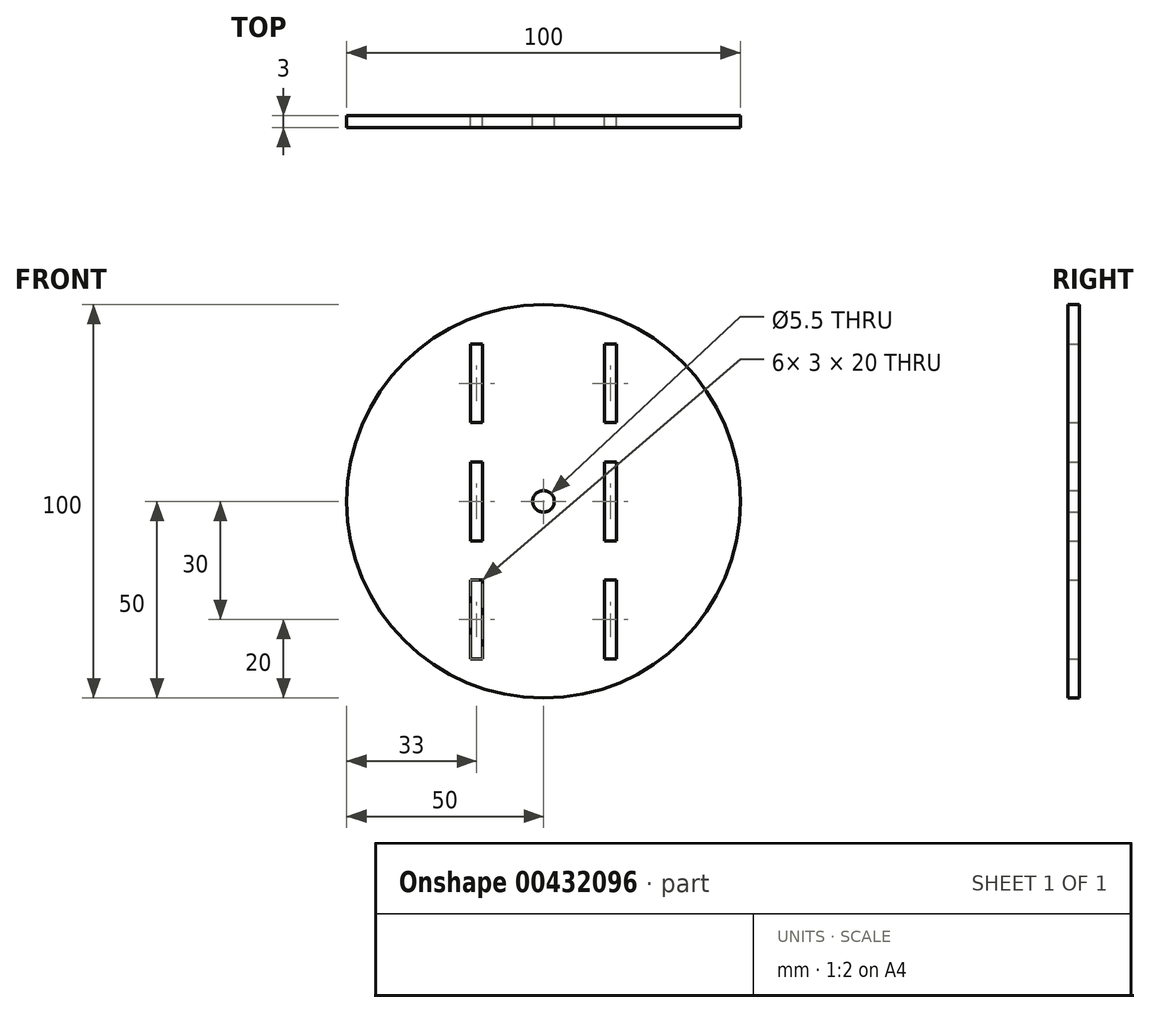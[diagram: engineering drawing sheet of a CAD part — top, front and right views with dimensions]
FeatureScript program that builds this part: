
annotation { "Feature Type Name" : "Feature", "Feature Type Description" : "" }
export const myFeature = defineFeature(function(context is Context, id is Id, definition is map)
    precondition{}
    {
        {
            var Q0;
            Q0=qCreatedBy(makeId("Front.planeOp"),FACE);
            var sketch = newSketch(context, id + "F0", { "sketchPlane" : qUnion([Q0])});
            skCircle(sketch, "E0", {"center": v(0, 0) * mm, "radius": 50 * mm});
            skCircle(sketch, "E1", {"center": v(0, 0) * mm, "radius": 2.75 * mm});
            skLineSegment(sketch, "E2.bottom", {"start": v(-18.5, 10) * mm, "end": v(-15.5, 10) * mm});
            skLineSegment(sketch, "E2.top", {"start": v(-18.5, -10) * mm, "end": v(-15.5, -10) * mm});
            skLineSegment(sketch, "E2.left", {"start": v(-18.5, 10) * mm, "end": v(-18.5, -10) * mm});
            skLineSegment(sketch, "E2.right", {"start": v(-15.5, 10) * mm, "end": v(-15.5, -10) * mm});
            skLineSegment(sketch, "E3.bottom", {"start": v(-18.5, -20) * mm, "end": v(-15.5, -20) * mm});
            skLineSegment(sketch, "E3.top", {"start": v(-18.5, -40) * mm, "end": v(-15.5, -40) * mm});
            skLineSegment(sketch, "E3.left", {"start": v(-18.5, -20) * mm, "end": v(-18.5, -40) * mm});
            skLineSegment(sketch, "E3.right", {"start": v(-15.5, -20) * mm, "end": v(-15.5, -40) * mm});
            skLineSegment(sketch, "E4.bottom", {"start": v(-18.5, 20) * mm, "end": v(-15.5, 20) * mm});
            skLineSegment(sketch, "E4.top", {"start": v(-18.5, 40) * mm, "end": v(-15.5, 40) * mm});
            skLineSegment(sketch, "E4.left", {"start": v(-18.5, 20) * mm, "end": v(-18.5, 40) * mm});
            skLineSegment(sketch, "E4.right", {"start": v(-15.5, 20) * mm, "end": v(-15.5, 40) * mm});
            skLineSegment(sketch, "E5.MirrorCS", {"start": v(18.5, 40) * mm, "end": v(15.5, 40) * mm});
            skLineSegment(sketch, "E6.MirrorCS", {"start": v(18.5, 20) * mm, "end": v(15.5, 20) * mm});
            skLineSegment(sketch, "E7.MirrorCS", {"start": v(18.5, 10) * mm, "end": v(15.5, 10) * mm});
            skLineSegment(sketch, "E8.MirrorCS", {"start": v(18.5, -10) * mm, "end": v(15.5, -10) * mm});
            skLineSegment(sketch, "E9.MirrorCS", {"start": v(18.5, -40) * mm, "end": v(15.5, -40) * mm});
            skLineSegment(sketch, "E10.MirrorCS", {"start": v(18.5, -20) * mm, "end": v(15.5, -20) * mm});
            skLineSegment(sketch, "E11.MirrorCS", {"start": v(15.5, 20) * mm, "end": v(15.5, 40) * mm});
            skLineSegment(sketch, "E12.MirrorCS", {"start": v(18.5, 20) * mm, "end": v(18.5, 40) * mm});
            skLineSegment(sketch, "E13.MirrorCS", {"start": v(18.5, 10) * mm, "end": v(18.5, -10) * mm});
            skLineSegment(sketch, "E14.MirrorCS", {"start": v(15.5, -20) * mm, "end": v(15.5, -40) * mm});
            skLineSegment(sketch, "E15.MirrorCS", {"start": v(15.5, 10) * mm, "end": v(15.5, -10) * mm});
            skLineSegment(sketch, "E16.MirrorCS", {"start": v(18.5, -20) * mm, "end": v(18.5, -40) * mm});
            skSolve(sketch);
        }
        {
            var Q0;
            Q0=makeQuery(id+"F0.imprint","IMPRINT",FACE,{"disambiguationData":[TD([[makeQuery(id+"F0.imprint","IMPRINT",EDGE,{"derivedFrom":sQuery(id+"F0.wireOp",EDGE,"E0")}),1.0]])]});
            extrude(context, id + "F1", {"entities" : qUnion([Q0]), "depth" : 3 * mm});
        }
    });
